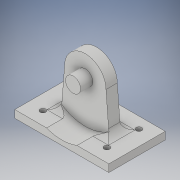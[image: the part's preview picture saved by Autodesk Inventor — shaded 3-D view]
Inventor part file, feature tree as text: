
AUTODESK INVENTOR PART (.ipt)
format: ipt  version: 2017 (Build 210142000, 142)  size: 172,544 bytes
history: native  units: in
note: dims shown in document units (in); Inventor stores cm internally (conversion verified against a paired STEP export)
features: sketch x7, extrude x5, fillet x1
ambient origin geometry x8: Origin, YZ Plane, XZ Plane, XY Plane, X Axis, Y Axis, Z Axis, Center Point
bodies: Solid1 (feature_tree)
feature tree (13):
  extrude  "Extrusion1"  Depth=0.9843in
  extrude  "Extrusion2"  Depth=0.5118in
  extrude  "Extrusion3"  Depth=0.315in
  fillet  "Fillet1"  Radius=0.2559in
  sketch  "Sketch4"  dims[d9=1.9685in d10=1.1811in]
  sketch  "Sketch5"  dims[d11=0.9843in d12=0.7283in]
  sketch  "Sketch6"  dims[d13=0.1575in d14=0.0in]
  extrude  "Extrusion4"  Depth=1.1811in
  extrude  "Extrusion5"  Depth=0.7283in
  sketch  "Sketch1"  dims[d0=0.8661in d1=0.9843in]
  sketch  "Sketch2"  dims[d2=0.5118in d3=0.5118in]
  sketch  "Sketch3"  dims[d4=0.2362in d5=0.0in d6=0.315in d7=0.2559in d8=0.0in]
  sketch  "Sketch7"  dims[d15=0.1575in d16=0.1181in d17=0.1181in d18=0.1181in d19=0.1181in d20=0.315in d21=0.2362in d22=0.2362in d23=0.315in d24=0.315in d25=0.2756in d26=0.2756in d27=0.315in d28=0.3937in d29=0.0in d30=1.7717in d31=0.315in d32=0.5118in d33=0.0in]
